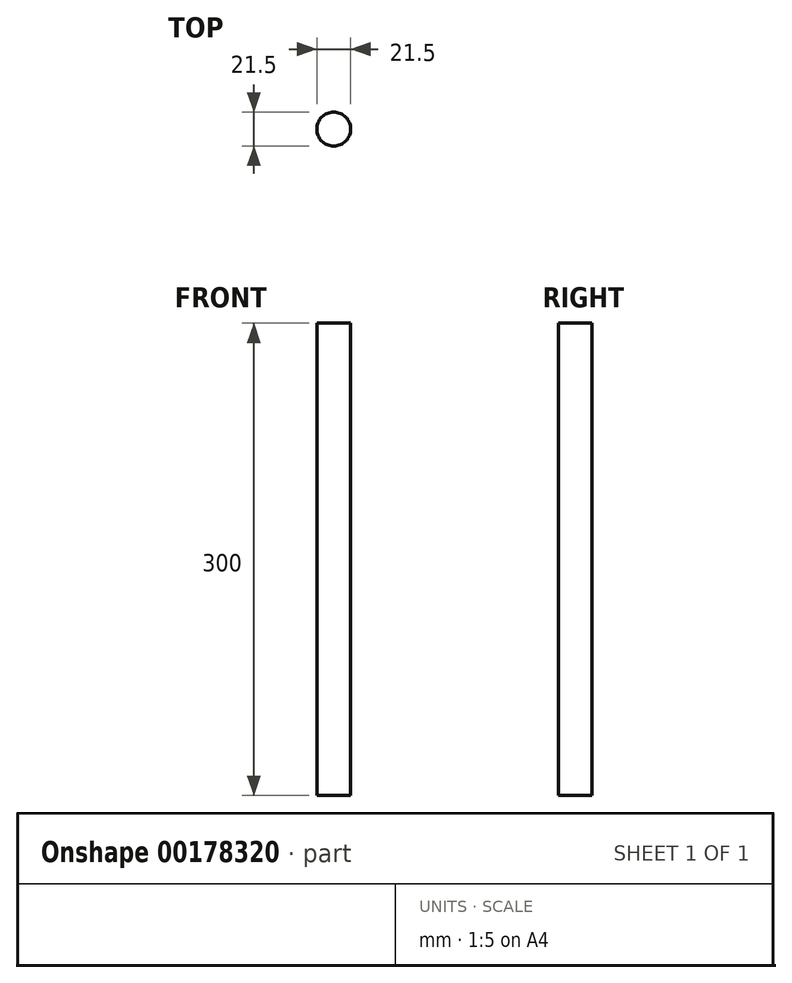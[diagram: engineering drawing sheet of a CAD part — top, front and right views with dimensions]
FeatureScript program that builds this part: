
annotation { "Feature Type Name" : "Feature", "Feature Type Description" : "" }
export const myFeature = defineFeature(function(context is Context, id is Id, definition is map)
    precondition{}
    {
        {
            var Q0;
            Q0=qCreatedBy(makeId("Top.planeOp"),FACE);
            var sketch = newSketch(context, id + "F0", { "sketchPlane" : qUnion([Q0])});
            skCircle(sketch, "E0", {"center": v(0, 0) * mm, "radius": 10.75 * mm});
            skSolve(sketch);
        }
        {
            var Q0;
            Q0 = qSketchRegion(id + "F0", true);
            extrude(context, id + "F1", {"entities" : qUnion([Q0]), "depth" : 300 * mm});
        }
    });
